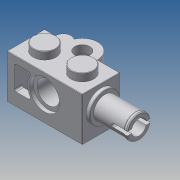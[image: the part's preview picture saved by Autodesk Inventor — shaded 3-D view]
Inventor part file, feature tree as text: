
AUTODESK INVENTOR PART (.ipt)
format: ipt  version: 2022.2 (Build 262287000, 287)  size: 347,648 bytes
history: native  units: in
note: dims shown in document units (in); Inventor stores cm internally (conversion verified against a paired STEP export)
features: extrude x10, sketch x6, revolve x1, fillet x1
ambient origin geometry x8: Origin, YZ Plane, XZ Plane, XY Plane, X Axis, Y Axis, Z Axis, Center Point
bodies: Solid1 (feature_tree)
feature tree (18):
  sketch  "Sketch2"  dims[d6=0.0in d8=0.0in]
  extrude  "Extrusion1"  TaperAngle=0.0deg  [1 undecoded]
  extrude  "Extrusion2"  TaperAngle=0.0deg  [1 undecoded]
  extrude  "Extrusion3"  Depth=0.6299in
  extrude  "Extrusion4"  Depth=0.0157in
  extrude  "Extrusion5"  Depth=0.126in
  sketch  "Sketch5"  dims[d27=0.315in d28=0.0157in]
  revolve  "Revolution1"  Angle=90.0deg
  extrude  "Extrusion6"  Depth=0.3937in TaperAngle=0.0deg
  sketch  "Sketch6"  dims[d29=0.315in d35=0.126in]
  extrude  "Extrusion7"  Depth=0.063in
  extrude  "Extrusion8"  Depth=0.189in
  extrude  "Extrusion9"  Depth=0.252in
  extrude  "Extrusion10"  Depth=0.2205in
  fillet  "Fillet1"  Radius=0.315in
  sketch  "Sketch3"  dims[d10=0.0in d19=0.0in]
  sketch  "Sketch4"  dims[d25=0.0in d26=0.6299in]
  sketch  "Sketch7"  dims[d37=0.315in d39=90.0deg d42=0.3937in d43=0.0in d44=0.063in d45=0.189in d46=0.252in d47=0.2205in d49=0.315in d50=0.0in d51=0.315in d52=0.0in d53=0.0315in d54=0.0in d55=0.1417in d56=45.0deg d57=0.063in d58=0.126in d59=0.0in]
note: 2 required parameter values undecoded (feature->parameter linkage not recoverable at this tier; creation-order binding heuristic only, values carry confidence <= 0.55)
